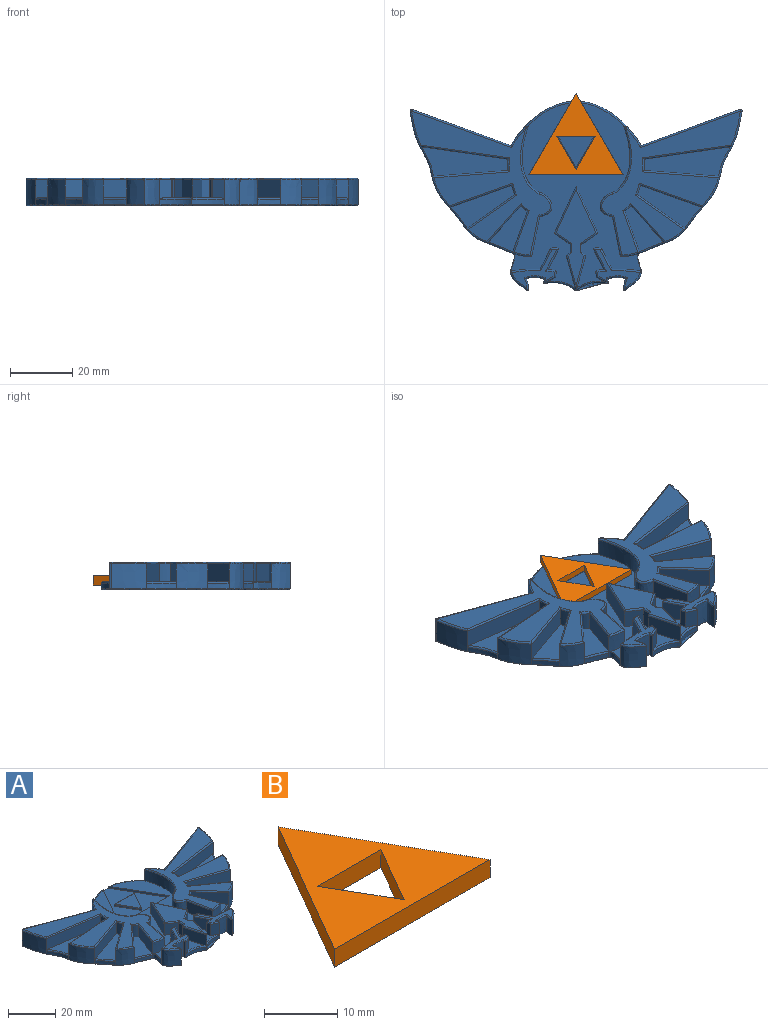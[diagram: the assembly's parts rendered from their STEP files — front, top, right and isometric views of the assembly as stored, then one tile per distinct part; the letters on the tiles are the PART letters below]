
ASSEMBLY  parts=2 mates=1
PART A: 226 faces, bbox 106.9x61.8x9.2 mm
  f0: extruded ~16.36x8.27mm, area 31.6mm2, adj f1,f63,f95,f100,f149,f215
  f1: extruded ~16.36x8.27mm, area 31.6mm2, adj f0,f15,f95,f99,f150,f213
  f2: plane 12.1x10.9mm, normal (0.74,-0.67,0), area 93.8mm2, adj f3,f19,f49,f152,f166
  f3: extruded ~5.8x1.99mm, area 15.4mm2, adj f2,f4,f49,f167
  f4: plane 13.49x6.32mm, normal (-0.94,0.34,0), area 83.1mm2, adj f3,f20,f49,f152,f169
  f5: plane 20.09x7.23mm, normal (0.34,-0.94,0), area 123.2mm2, adj f6,f18,f47,f153,f174
  f6: extruded ~5.8x3mm, area 18.4mm2, adj f5,f7,f47,f172
  f7: plane 15.58x11.01mm, normal (-0.58,0.82,0), area 110.6mm2, adj f6,f19,f47,f153,f170
  f8: plane 28.3x6.45mm, normal (-0.14,-0.99,0), area 165.1mm2, adj f9,f17,f45,f154,f182
  f9: extruded ~5.8x3.6mm, area 20.9mm2, adj f8,f10,f45,f180
  f10: plane 24.39x6.32mm, normal (-0.08,1,0), area 141.8mm2, adj f9,f18,f45,f154,f178
  f11: plane 6.49x1.24mm, normal (-0.05,1,0), area 6.2mm2, adj f14,f15,f43,f150,f179
  f12: plane 12.72x5.8mm, normal (0.98,-0.2,0), area 75.3mm2, adj f13,f20,f43,f173
  f13: extruded ~7.69x5.8mm, area 68.7mm2, adj f12,f14,f43,f175
  f14: extruded ~21.11x5.8mm, area 135.7mm2, adj f11,f13,f43,f177
  f15: extruded ~8.02x6.02mm, area 60.4mm2, adj f1,f11,f16,f181,f211
  f16: plane 31.67x11.59mm, normal (0.34,0.94,0), area 270.4mm2, adj f15,f183,f186,f209
  f17: extruded ~11.29x8.02mm, area 94.3mm2, adj f8,f44,f184,f186,f205
  f18: extruded ~10.01x8.02mm, area 92.9mm2, adj f5,f10,f44,f46,f176,f201
  f19: extruded ~8.02x6.74mm, area 66.1mm2, adj f2,f7,f46,f48,f168,f197
  f20: extruded ~8.02x6.24mm, area 37.2mm2, adj f4,f12,f41,f43,f48,f171,f188,f193
  f21: plane 46.11x44.47mm, normal (0,0,1), area 636.8mm2, adj f166,f167,f168,f169,f170,f171,f172,f173
  f22: plane 106.15x60.51mm, normal (0,0,-1), area 3849.3mm2, adj f189,f190,f191,f192,f193,f194,f195,f196
  f23: plane 15.22x7.01mm, normal (-0.91,0.42,0), area 97.2mm2, adj f24,f43,f70,f124
  f24: plane 5.8x5.11mm, normal (-0.56,-0.83,0), area 35.7mm2, adj f23,f25,f43,f122
  f25: plane 5.8x2.55mm, normal (-1,0,0), area 14.8mm2, adj f24,f26,f43,f120
  f26: plane 5.8x1.26mm, normal (-0.63,0.77,0), area 9.4mm2, adj f25,f27,f43,f118
  f27: plane 11.58x6.52mm, normal (-0.96,-0.27,0), area 68.5mm2, adj f26,f43,f74,f116,f151
  f28: plane 30.53x12.76mm, normal (0,0,1), area 151.1mm2, adj f116,f117,f118,f119,f120,f121,f122,f123
  f29: plane 5.8x2mm, normal (0.98,-0.17,0), area 11.8mm2, adj f30,f39,f43,f162
  f30: extruded ~5.8x2.72mm, area 16.1mm2, adj f29,f31,f43,f160
  f31: plane 6.66x5.8mm, normal (0.89,-0.46,0), area 43.5mm2, adj f30,f32,f43,f158
  f32: extruded ~5.8x2.7mm, area 16.5mm2, adj f31,f33,f43,f156
  f33: plane 6.49x5.8mm, normal (-0.89,0.46,0), area 42.5mm2, adj f32,f34,f43,f155
  f34: extruded ~9.39x5.9mm, area 54.7mm2, adj f33,f35,f43,f157,f188
  f35: extruded ~8.02x6.32mm, area 70.4mm2, adj f34,f36,f41,f159,f189
  f36: extruded ~8.02x3.9mm, area 31.9mm2, adj f35,f37,f161,f190
  f37: extruded ~8.02x5.64mm, area 46mm2, adj f36,f38,f163,f192
  f38: plane 8.02x1.47mm, normal (-1,0,0), area 11.8mm2, adj f37,f39,f42,f165,f194
  f39: plane 6.57x3.94mm, normal (0.46,-0.89,0), area 24.1mm2, adj f29,f38,f43,f151,f164
  f40: plane 14.28x12.37mm, normal (0,0,1), area 42.8mm2, adj f155,f156,f157,f158,f159,f160,f161,f162
  f41: extruded ~5.73x2.12mm, area 13mm2, adj f20,f35,f188,f191
  f42: extruded ~10.25x2.65mm, area 18.8mm2, adj f38,f88,f151,f196
  f43: plane 59.34x41.84mm, normal (0,0,1), area 930.7mm2, adj f11,f12,f13,f14,f20,f23,f24,f25
  f44: extruded ~9.61x3.92mm, area 18mm2, adj f17,f18,f154,f203
  f45: plane 27.66x9.48mm, normal (0,0,1), area 162.3mm2, adj f8,f9,f10,f154
  f46: extruded ~6.85x5.47mm, area 15.1mm2, adj f18,f19,f153,f199
  f47: plane 20.52x13.71mm, normal (0,0,1), area 111.7mm2, adj f5,f6,f7,f153
  f48: extruded ~7.96x3.2mm, area 14.8mm2, adj f19,f20,f152,f195
  f49: plane 14.74x12.43mm, normal (0,0,1), area 78mm2, adj f2,f3,f4,f152
  f50: plane 12.1x10.9mm, normal (-0.74,-0.67,0), area 93.8mm2, adj f51,f67,f94,f104,f143
  f51: extruded ~5.8x1.99mm, area 15.4mm2, adj f50,f52,f94,f145
  f52: plane 13.49x6.32mm, normal (0.94,0.34,0), area 83.1mm2, adj f51,f68,f94,f104,f146
  f53: plane 20.09x7.23mm, normal (-0.34,-0.94,0), area 123.2mm2, adj f54,f66,f92,f103,f135
  f54: extruded ~5.8x3mm, area 18.4mm2, adj f53,f55,f92,f137
  f55: plane 15.58x11.01mm, normal (0.58,0.82,0), area 110.6mm2, adj f54,f67,f92,f103,f139
  f56: plane 28.3x6.45mm, normal (0.14,-0.99,0), area 165.1mm2, adj f57,f65,f90,f126,f147
  f57: extruded ~5.8x3.6mm, area 20.9mm2, adj f56,f58,f90,f129
  f58: plane 24.39x6.32mm, normal (0.08,1,0), area 141.8mm2, adj f57,f66,f90,f131,f147
  f59: plane 6.49x1.24mm, normal (0.05,1,0), area 6.2mm2, adj f43,f62,f63,f136,f149
  f60: plane 12.72x5.8mm, normal (-0.98,-0.2,0), area 75.3mm2, adj f43,f61,f68,f142
  f61: extruded ~7.69x5.8mm, area 68.7mm2, adj f43,f60,f62,f140
  f62: extruded ~21.11x5.8mm, area 135.7mm2, adj f43,f59,f61,f138
  f63: extruded ~8.02x6.02mm, area 60.4mm2, adj f0,f59,f64,f134,f217
  f64: plane 31.67x11.59mm, normal (-0.34,0.94,0), area 270.4mm2, adj f63,f127,f132,f219
  f65: extruded ~11.29x8.02mm, area 94.3mm2, adj f56,f89,f127,f128,f222
  f66: extruded ~10.01x8.02mm, area 92.9mm2, adj f53,f58,f89,f91,f133,f218
  f67: extruded ~8.02x6.74mm, area 66.1mm2, adj f50,f55,f91,f93,f141,f214
  f68: extruded ~8.02x6.24mm, area 37.2mm2, adj f43,f52,f60,f87,f93,f144,f187,f210
  f69: plane 46.11x44.47mm, normal (0,0,1), area 636.8mm2, adj f126,f128,f129,f131,f132,f133,f134,f135
  f70: plane 15.22x7.01mm, normal (0.91,0.42,0), area 97.2mm2, adj f23,f43,f71,f125
  f71: plane 5.8x5.11mm, normal (0.56,-0.83,0), area 35.7mm2, adj f43,f70,f72,f123
  f72: plane 5.8x2.55mm, normal (1,0,0), area 14.8mm2, adj f43,f71,f73,f121
  f73: plane 5.8x1.26mm, normal (0.63,0.77,0), area 9.4mm2, adj f43,f72,f74,f119
  f74: plane 11.58x6.52mm, normal (0.96,-0.27,0), area 68.5mm2, adj f27,f43,f73,f117,f148
  f75: plane 5.8x2mm, normal (-0.98,-0.17,0), area 11.8mm2, adj f43,f76,f85,f107
  f76: extruded ~5.8x2.72mm, area 16.1mm2, adj f43,f75,f77,f109
  f77: plane 6.66x5.8mm, normal (-0.89,-0.46,0), area 43.5mm2, adj f43,f76,f78,f111
  f78: extruded ~5.8x2.7mm, area 16.5mm2, adj f43,f77,f79,f113
  f79: plane 6.49x5.8mm, normal (0.89,0.46,0), area 42.5mm2, adj f43,f78,f80,f115
  f80: extruded ~9.39x5.9mm, area 54.7mm2, adj f43,f79,f81,f114,f187
  f81: extruded ~8.02x6.32mm, area 70.4mm2, adj f80,f82,f87,f112,f206
  f82: extruded ~8.02x3.9mm, area 31.9mm2, adj f81,f83,f110,f204
  f83: extruded ~8.02x5.64mm, area 46mm2, adj f82,f84,f108,f202
  f84: plane 8.02x1.47mm, normal (1,0,0), area 11.8mm2, adj f83,f85,f88,f106,f200
  f85: plane 6.57x3.94mm, normal (-0.46,-0.89,0), area 24.1mm2, adj f43,f75,f84,f105,f148
  f86: plane 14.28x12.37mm, normal (0,0,1), area 42.8mm2, adj f105,f106,f107,f108,f109,f110,f111,f112
  f87: extruded ~5.73x2.12mm, area 13mm2, adj f68,f81,f187,f208
  f88: extruded ~10.25x2.65mm, area 18.8mm2, adj f42,f84,f148,f198
  f89: extruded ~9.61x3.92mm, area 18mm2, adj f65,f66,f147,f220
  f90: plane 27.66x9.48mm, normal (0,0,1), area 162.3mm2, adj f56,f57,f58,f147
  f91: extruded ~6.85x5.47mm, area 15.1mm2, adj f66,f67,f103,f216
  f92: plane 20.52x13.71mm, normal (0,0,1), area 111.7mm2, adj f53,f54,f55,f103
  f93: extruded ~7.96x3.2mm, area 14.8mm2, adj f67,f68,f104,f212
  f94: plane 14.74x12.43mm, normal (0,0,1), area 78mm2, adj f50,f51,f52,f104
  f95: plane 30.17x23.48mm, normal (0,0,1), area 327.1mm2, adj f0,f1,f96,f97,f98,f99,f100,f101
  f96: plane 12.06x0.8mm, normal (0,1,0), area 9.6mm2, adj f95,f97,f98,f225
  f97: plane 10.44x6.03mm, normal (0.87,-0.5,0), area 9.6mm2, adj f95,f96,f98,f223
  f98: plane 10.44x6.03mm, normal (-0.87,-0.5,0), area 9.6mm2, adj f95,f96,f97,f224
  f99: plane 23.53x13.65mm, normal (0.87,-0.5,0), area 26.9mm2, adj f1,f43,f95,f101,f150
  f100: plane 23.53x13.65mm, normal (-0.87,-0.5,0), area 26.9mm2, adj f0,f43,f95,f101,f149
  f101: plane 30.17x1mm, normal (0,1,0), area 30.2mm2, adj f43,f95,f99,f100
  f102: plane 11.36x9.84mm, normal (0,0,1), area 55.9mm2, adj f223,f224,f225
  f103: bspline ~9.3x7.65mm, area 6.8mm2, adj f53,f55,f91,f92
  f104: bspline ~8.73x3.87mm, area 6.7mm2, adj f50,f52,f93,f94
  f105: cylinder r=0.5mm len=3.9mm, axis (0.89,-0.46,0), area 2.8mm2, adj f85,f86,f106,f107
  f106: cylinder r=0.5mm len=1.83mm, axis (0,1,0), area 1mm2, adj f84,f86,f105,f108
  f107: cylinder r=0.5mm len=2.09mm, axis (0.17,-0.98,0), area 1.3mm2, adj f75,f86,f105,f109
  f108: bspline ~7.65x1.27mm, area 5mm2, adj f83,f86,f106,f110
  f109: bspline ~5.74x1.19mm, area 2.3mm2, adj f76,f86,f107,f111
  f110: bspline ~4.71x1.42mm, area 2.9mm2, adj f82,f86,f108,f112
  f111: cylinder r=0.5mm len=7.58mm, axis (0.46,-0.89,0), area 6mm2, adj f77,f86,f109,f113
  f112: bspline ~6.79x6.06mm, area 6.2mm2, adj f81,f86,f110,f114
  f113: bspline ~2.79x0.83mm, area 1.8mm2, adj f78,f86,f111,f115
  f114: bspline ~11.97x1.21mm, area 7.3mm2, adj f80,f86,f112,f115
  f115: cylinder r=0.5mm len=7mm, axis (-0.46,0.89,0), area 5.8mm2, adj f79,f86,f113,f114
  f116: cylinder r=0.5mm len=11.49mm, axis (-0.27,0.96,0), area 8.4mm2, adj f27,f28,f117,f118
  f117: cylinder r=0.5mm len=11.49mm, axis (0.27,0.96,0), area 8.4mm2, adj f28,f74,f116,f119
  f118: cylinder r=0.5mm len=1.76mm, axis (0.77,0.63,0), area 1.2mm2, adj f26,f28,f116,f120
  f119: cylinder r=0.5mm len=1.76mm, axis (-0.77,0.63,0), area 1.2mm2, adj f28,f73,f117,f121
  f120: cylinder r=0.5mm len=3.06mm, axis (0,1,0), area 2.2mm2, adj f25,f28,f118,f122
  f121: cylinder r=0.5mm len=3.06mm, axis (0,1,0), area 2.2mm2, adj f28,f72,f119,f123
  f122: cylinder r=0.5mm len=5.61mm, axis (-0.83,0.56,0), area 4.8mm2, adj f24,f28,f120,f124
  f123: cylinder r=0.5mm len=5.61mm, axis (0.83,0.56,0), area 4.8mm2, adj f28,f71,f121,f125
  f124: cylinder r=0.5mm len=15.43mm, axis (0.42,0.91,0), area 12.6mm2, adj f23,f28,f122,f125
  f125: cylinder r=0.5mm len=15.43mm, axis (-0.42,0.91,0), area 12.6mm2, adj f28,f70,f123,f124
  f126: cylinder r=0.5mm len=28.67mm, axis (0.99,0.14,0), area 22.4mm2, adj f56,f69,f128,f129
  f127: cylinder r=0.5mm len=8.02mm, axis (0,0,-1), area 8.3mm2, adj f64,f65,f130,f221
  f128: bspline ~12.06x3.75mm, area 9.1mm2, adj f65,f69,f126,f130
  f129: bspline ~6.29x0.94mm, area 3.2mm2, adj f57,f69,f126,f131
  f130: sphere r=0.5mm, area 0.5mm2, adj f127,f128,f132
  f131: cylinder r=0.5mm len=24.94mm, axis (-1,0.08,0), area 19.2mm2, adj f58,f69,f129,f133
  f132: cylinder r=0.5mm len=32.28mm, axis (-0.94,-0.34,0), area 26.7mm2, adj f64,f69,f130,f134
  f133: bspline ~11.69x7.18mm, area 8.7mm2, adj f66,f69,f131,f135
  f134: bspline ~8.3x6.14mm, area 6mm2, adj f63,f69,f132,f136
  f135: cylinder r=0.5mm len=20.69mm, axis (0.94,-0.34,0), area 16.8mm2, adj f53,f69,f133,f137
  f136: cylinder r=0.5mm len=1.07mm, axis (-1,0.05,0), area 0.5mm2, adj f59,f69,f134,f138
  f137: bspline ~5.91x2.28mm, area 2.8mm2, adj f54,f69,f135,f139
  f138: bspline ~22.13x6.69mm, area 18.3mm2, adj f62,f69,f136,f140
  f139: cylinder r=0.5mm len=16.18mm, axis (-0.82,0.58,0), area 14.9mm2, adj f55,f69,f137,f141
  f140: bspline ~7.84x4.61mm, area 9.1mm2, adj f61,f69,f138,f142
  f141: bspline ~7.4x5.2mm, area 6.1mm2, adj f67,f69,f139,f143
  f142: cylinder r=0.5mm len=13.15mm, axis (0.2,-0.98,0), area 10.2mm2, adj f60,f69,f140,f144
  f143: cylinder r=0.5mm len=12.81mm, axis (0.67,-0.74,0), area 12.8mm2, adj f50,f69,f141,f145
  f144: bspline ~8.06x1.99mm, area 4.6mm2, adj f68,f69,f142,f146
  f145: bspline ~4.45x4.41mm, area 2.4mm2, adj f51,f69,f143,f146
  f146: cylinder r=0.5mm len=14.02mm, axis (-0.34,0.94,0), area 11.2mm2, adj f52,f69,f144,f145
  f147: bspline ~10.93x4.92mm, area 8.1mm2, adj f56,f58,f89,f90
  f148: bspline ~11.62x3.77mm, area 7.9mm2, adj f43,f74,f85,f88
  f149: bspline ~15.86x9.04mm, area 13.1mm2, adj f0,f43,f59,f100
  f150: bspline ~15.86x9.04mm, area 13.1mm2, adj f1,f11,f43,f99
  f151: bspline ~11.62x3.77mm, area 7.9mm2, adj f27,f39,f42,f43
  f152: bspline ~8.73x3.87mm, area 6.7mm2, adj f2,f4,f48,f49
  f153: bspline ~9.3x7.65mm, area 6.8mm2, adj f5,f7,f46,f47
  f154: bspline ~10.93x4.92mm, area 8.1mm2, adj f8,f10,f44,f45
  f155: cylinder r=0.5mm len=7mm, axis (0.46,0.89,0), area 5.8mm2, adj f33,f40,f156,f157
  f156: bspline ~2.79x0.83mm, area 1.8mm2, adj f32,f40,f155,f158
  f157: bspline ~11.97x1.21mm, area 7.3mm2, adj f34,f40,f155,f159
  f158: cylinder r=0.5mm len=7.58mm, axis (-0.46,-0.89,0), area 6mm2, adj f31,f40,f156,f160
  f159: bspline ~6.79x6.06mm, area 6.2mm2, adj f35,f40,f157,f161
  f160: bspline ~5.74x1.19mm, area 2.3mm2, adj f30,f40,f158,f162
  f161: bspline ~4.71x1.42mm, area 2.9mm2, adj f36,f40,f159,f163
  f162: cylinder r=0.5mm len=2.09mm, axis (-0.17,-0.98,0), area 1.3mm2, adj f29,f40,f160,f164
  f163: bspline ~7.65x1.27mm, area 5mm2, adj f37,f40,f161,f165
  f164: cylinder r=0.5mm len=3.9mm, axis (-0.89,-0.46,0), area 2.8mm2, adj f39,f40,f162,f165
  f165: cylinder r=0.5mm len=1.83mm, axis (0,1,0), area 1mm2, adj f38,f40,f163,f164
  f166: cylinder r=0.5mm len=12.81mm, axis (-0.67,-0.74,0), area 12.8mm2, adj f2,f21,f167,f168
  f167: bspline ~4.45x4.41mm, area 2.4mm2, adj f3,f21,f166,f169
  f168: bspline ~7.4x5.2mm, area 6.1mm2, adj f19,f21,f166,f170
  f169: cylinder r=0.5mm len=14.02mm, axis (0.34,0.94,0), area 11.2mm2, adj f4,f21,f167,f171
  f170: cylinder r=0.5mm len=16.18mm, axis (0.82,0.58,0), area 14.9mm2, adj f7,f21,f168,f172
  f171: bspline ~8.06x1.99mm, area 4.6mm2, adj f20,f21,f169,f173
  f172: bspline ~5.91x2.28mm, area 2.8mm2, adj f6,f21,f170,f174
  f173: cylinder r=0.5mm len=13.15mm, axis (-0.2,-0.98,0), area 10.2mm2, adj f12,f21,f171,f175
  f174: cylinder r=0.5mm len=20.69mm, axis (-0.94,-0.34,0), area 16.8mm2, adj f5,f21,f172,f176
  f175: bspline ~7.84x4.61mm, area 9.1mm2, adj f13,f21,f173,f177
  f176: bspline ~11.69x7.18mm, area 8.7mm2, adj f18,f21,f174,f178
  f177: bspline ~22.13x6.69mm, area 18.3mm2, adj f14,f21,f175,f179
  f178: cylinder r=0.5mm len=24.94mm, axis (1,0.08,0), area 19.2mm2, adj f10,f21,f176,f180
  f179: cylinder r=0.5mm len=1.07mm, axis (1,0.05,0), area 0.5mm2, adj f11,f21,f177,f181
  f180: bspline ~6.29x0.94mm, area 3.2mm2, adj f9,f21,f178,f182
  f181: bspline ~8.3x6.14mm, area 6mm2, adj f15,f21,f179,f183
  f182: cylinder r=0.5mm len=28.67mm, axis (-0.99,0.14,0), area 22.4mm2, adj f8,f21,f180,f184
  f183: cylinder r=0.5mm len=32.28mm, axis (0.94,-0.34,0), area 26.7mm2, adj f16,f21,f181,f185
  f184: bspline ~12.06x3.75mm, area 9.1mm2, adj f17,f21,f182,f185
  f185: sphere r=0.5mm, area 0.5mm2, adj f183,f184,f186
  f186: cylinder r=0.5mm len=8.02mm, axis (0,0,-1), area 8.3mm2, adj f16,f17,f185,f207
  f187: bspline ~6x1.26mm, area 0.9mm2, adj f43,f68,f80,f87
  f188: bspline ~6x1.26mm, area 0.9mm2, adj f20,f34,f41,f43
  f189: bspline ~6.33x5.78mm, area 3.6mm2, adj f22,f35,f190,f191
  f190: bspline ~4.55x1.13mm, area 1.6mm2, adj f22,f36,f189,f192
  f191: bspline ~6.2x1.49mm, area 2.7mm2, adj f22,f41,f189,f193
  f192: bspline ~6.94x1.02mm, area 2.6mm2, adj f22,f37,f190,f194
  f193: bspline ~0.32x0.31mm, area 0mm2, adj f20,f22,f191,f195
  f194: plane 1.69x0.3mm, normal (-0.71,0,-0.71), area 0.6mm2, adj f22,f38,f192,f196
  f195: bspline ~8.46x3.61mm, area 3.6mm2, adj f22,f48,f193,f197
  f196: bspline ~11.47x3.47mm, area 4.5mm2, adj f22,f42,f194,f198
  f197: bspline ~7.48x5.18mm, area 3.4mm2, adj f19,f22,f195,f199
  f198: bspline ~11.47x3.47mm, area 4.5mm2, adj f22,f88,f196,f200
  f199: bspline ~7.05x5.72mm, area 3.7mm2, adj f22,f46,f197,f201
  f200: plane 1.69x0.3mm, normal (0.71,0,-0.71), area 0.6mm2, adj f22,f84,f198,f202
  f201: bspline ~10.62x5.86mm, area 4.9mm2, adj f18,f22,f199,f203
  f202: bspline ~6.34x0.86mm, area 2.6mm2, adj f22,f83,f200,f204
  f203: bspline ~10.74x4.57mm, area 4.4mm2, adj f22,f44,f201,f205
  f204: bspline ~4.55x1.13mm, area 1.6mm2, adj f22,f82,f202,f206
  f205: bspline ~11.86x3.63mm, area 5mm2, adj f17,f22,f203,f207
  f206: bspline ~6.33x5.78mm, area 3.6mm2, adj f22,f81,f204,f208
  f207: cone r=0.2mm half-angle=45deg, axis (0,0,1), area 0.3mm2, adj f22,f186,f205,f209
  f208: bspline ~6.2x1.49mm, area 2.7mm2, adj f22,f87,f206,f210
  f209: plane 31.93x11.97mm, normal (0.24,0.66,-0.71), area 14.4mm2, adj f16,f22,f207,f211
  f210: bspline ~0.32x0.31mm, area 0mm2, adj f22,f68,f208,f212
  f211: bspline ~7.04x5.23mm, area 3.2mm2, adj f15,f22,f209,f213
  f212: bspline ~8.46x3.61mm, area 3.6mm2, adj f22,f93,f210,f214
  f213: bspline ~17.94x9.18mm, area 8mm2, adj f1,f22,f211,f215
  f214: bspline ~7.48x5.18mm, area 3.4mm2, adj f22,f67,f212,f216
  f215: bspline ~17.94x9.18mm, area 8mm2, adj f0,f22,f213,f217
  f216: bspline ~7.05x5.72mm, area 3.7mm2, adj f22,f91,f214,f218
  f217: bspline ~7.04x5.23mm, area 3.2mm2, adj f22,f63,f215,f219
  f218: bspline ~10.62x5.86mm, area 4.9mm2, adj f22,f66,f216,f220
  f219: plane 31.93x11.97mm, normal (-0.24,0.66,-0.71), area 14.4mm2, adj f22,f64,f217,f221
  f220: bspline ~10.74x4.57mm, area 4.4mm2, adj f22,f89,f218,f222
  f221: cone r=0.2mm half-angle=45deg, axis (0,0,1), area 0.3mm2, adj f22,f127,f219,f222
  f222: bspline ~11.86x3.63mm, area 5mm2, adj f22,f65,f220,f221
  f223: cylinder r=0.2mm len=10.54mm, axis (0.5,0.87,0), area 3.7mm2, adj f97,f102,f224,f225
  f224: cylinder r=0.2mm len=10.54mm, axis (0.5,-0.87,0), area 3.7mm2, adj f98,f102,f223,f225
  f225: cylinder r=0.2mm len=12.06mm, axis (-1,0,0), area 3.7mm2, adj f96,f102,f223,f224
PART B: 8 faces, bbox 30x26x3 mm
  f0: plane 25.98x15mm, normal (0.87,0.5,0), area 90mm2, adj f1,f2,f3,f7
  f1: plane 25.98x15mm, normal (-0.87,0.5,0), area 90mm2, adj f0,f2,f3,f7
  f2: plane 30x3mm, normal (0,-1,0), area 90mm2, adj f0,f1,f3,f7
  f3: plane 30x25.98mm, normal (0,0,-1), area 325mm2, adj f0,f1,f2,f4,f5,f6
  f4: plane 12.23x3mm, normal (0,-1,0), area 36.7mm2, adj f3,f5,f6,f7
  f5: plane 10.59x6.11mm, normal (0.87,0.5,0), area 36.7mm2, adj f3,f4,f6,f7
  f6: plane 10.59x6.11mm, normal (-0.87,0.5,0), area 36.7mm2, adj f3,f4,f5,f7
  f7: plane 30x25.98mm, normal (0,0,1), area 325mm2, adj f0,f1,f2,f4,f5,f6
PLACE A at identity
PLACE B t=(0,20.62,1.52)mm
MATE fastened B.f3 <-> A.f95  axis (0,0,-1) through (0,20.62,1.52)mm
